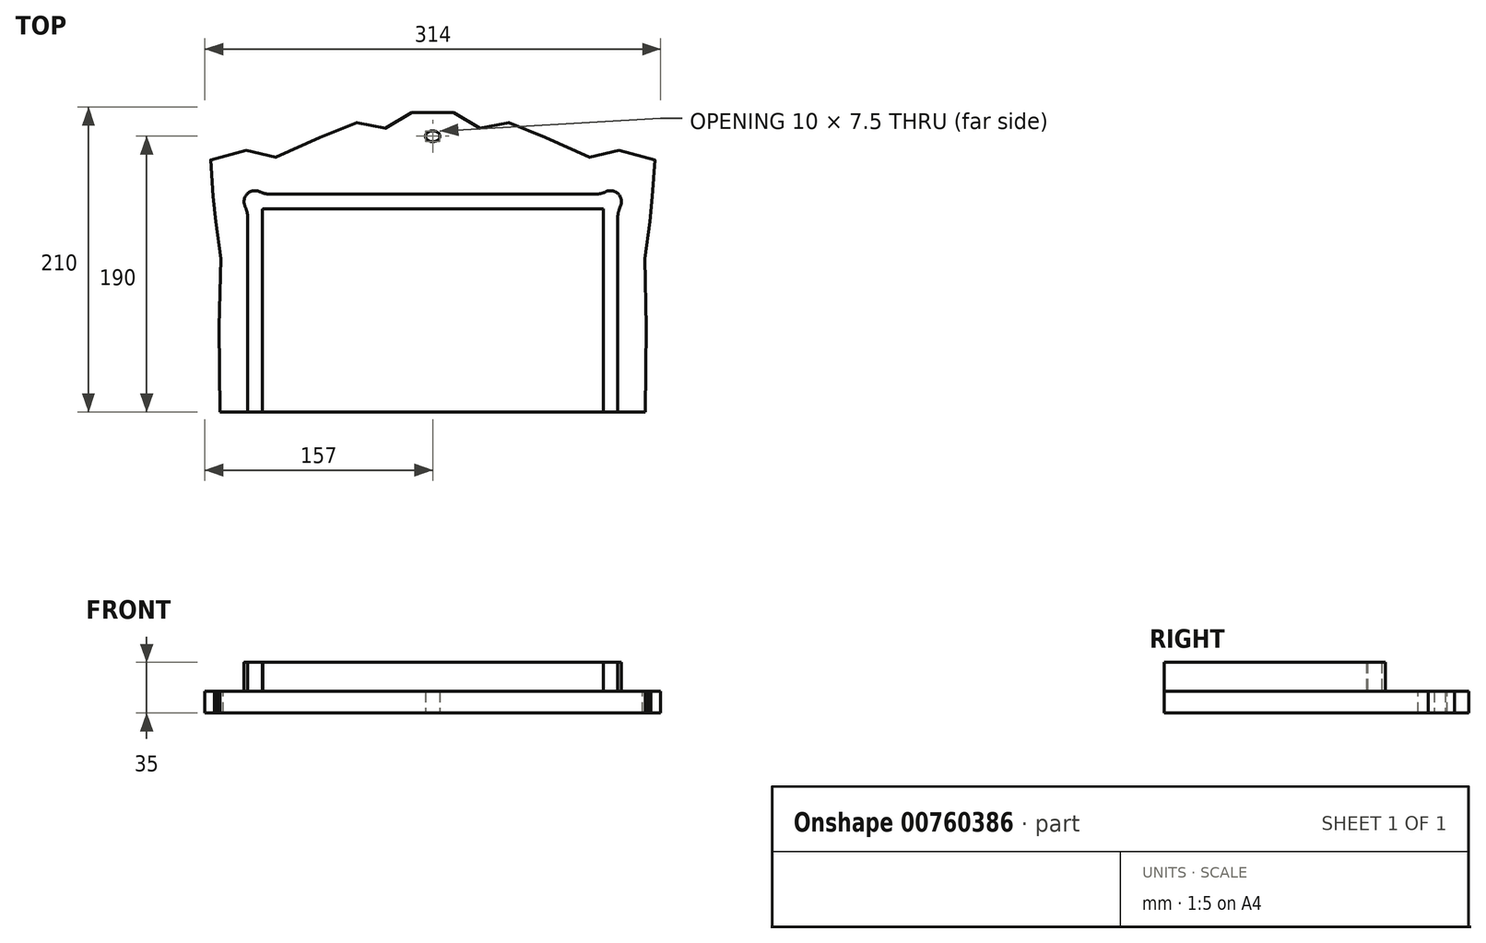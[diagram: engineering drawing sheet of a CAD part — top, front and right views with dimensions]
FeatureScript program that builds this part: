
annotation { "Feature Type Name" : "Feature", "Feature Type Description" : "" }
export const myFeature = defineFeature(function(context is Context, id is Id, definition is map)
    precondition{}
    {
        {
            var Q0;
            Q0=qCreatedBy(makeId("Top.planeOp"),FACE);
            var sketch = newSketch(context, id + "F0", { "sketchPlane" : qUnion([Q0])});
            skPoint(sketch, "E0", {"position": v(151.1, 154.93) * mm});
            skPoint(sketch, "E1", {"position": v(140, 77.47) * mm});
            skPoint(sketch, "E2", {"position": v(146.5, 0) * mm});
            skPoint(sketch, "E3", {"position": v(0, 210) * mm});
            skPoint(sketch, "E4", {"position": v(72.86, 179.48) * mm});
            skPoint(sketch, "E5", {"position": v(-38.35, 186.04) * mm});
            skPoint(sketch, "E6", {"position": v(-24.12, 200) * mm});
            skPoint(sketch, "E7", {"position": v(-154.5, 163.42) * mm});
            skLineSegment(sketch, "E8", {"start": v(0, 210) * mm, "end": v(0, -300) * mm, "construction": true});
            skPoint(sketch, "E9.MirrorP", {"position": v(-72.86, 179.48) * mm});
            skPoint(sketch, "E10.MirrorP", {"position": v(-151.1, 154.93) * mm});
            skPoint(sketch, "E11.MirrorP", {"position": v(-140, 77.47) * mm});
            skPoint(sketch, "E12.MirrorP", {"position": v(-146.5, 0) * mm});
            skPoint(sketch, "E13", {"position": v(0, 0) * mm});
            skPoint(sketch, "E14.MirrorP", {"position": v(154.5, 163.42) * mm});
            skPoint(sketch, "E15.MirrorP", {"position": v(38.35, 186.04) * mm});
            skPoint(sketch, "E16.MirrorP", {"position": v(24.12, 200) * mm});
            skPoint(sketch, "E17", {"position": v(-111.22, 185.44) * mm});
            skPoint(sketch, "E18.MirrorP", {"position": v(111.21, 185.44) * mm});
            skLineSegment(sketch, "E19", {"start": v(-146.5, 0) * mm, "end": v(146.5, 0) * mm});
            skPoint(sketch, "E20", {"position": v(0, 193.84) * mm});
            skPoint(sketch, "E21", {"position": v(-120.16, 190.34) * mm});
            skPoint(sketch, "E22", {"position": v(-131.3, 192.59) * mm});
            skPoint(sketch, "E23", {"position": v(-143.04, 189.12) * mm});
            skPoint(sketch, "E24", {"position": v(-150.16, 182.65) * mm});
            skPoint(sketch, "E25", {"position": v(-153.61, 176.08) * mm});
            skPoint(sketch, "E26", {"position": v(-154.92, 169.2) * mm});
            skPoint(sketch, "E27.MirrorP", {"position": v(120.16, 190.34) * mm});
            skPoint(sketch, "E28.MirrorP", {"position": v(131.3, 192.59) * mm});
            skPoint(sketch, "E29.MirrorP", {"position": v(143.04, 189.12) * mm});
            skPoint(sketch, "E30.MirrorP", {"position": v(150.16, 182.65) * mm});
            skPoint(sketch, "E31.MirrorP", {"position": v(153.61, 176.08) * mm});
            skPoint(sketch, "E32.MirrorP", {"position": v(154.92, 169.2) * mm});
            skFitSpline(sketch, "E33", {"points": [v(-146.5, 0) * mm, v(-140, 77.47) * mm, v(-151.1, 154.93) * mm, v(-154.5, 163.42) * mm, v(-154.92, 169.2) * mm, v(-153.61, 176.08) * mm, v(-150.16, 182.65) * mm, v(-143.04, 189.12) * mm, v(-131.3, 192.59) * mm, v(-120.16, 190.34) * mm, v(-111.22, 185.44) * mm, v(-72.87, 179.48) * mm, v(-38.35, 186.04) * mm, v(-24.12, 200) * mm, v(0, 210) * mm, v(24.12, 200) * mm, v(38.35, 186.04) * mm, v(72.86, 179.48) * mm, v(111.21, 185.44) * mm, v(120.16, 190.34) * mm, v(131.3, 192.59) * mm, v(143.04, 189.12) * mm, v(150.16, 182.65) * mm, v(153.61, 176.08) * mm, v(154.92, 169.2) * mm, v(154.5, 163.42) * mm, v(151.1, 154.93) * mm, v(140, 77.47) * mm, v(146.5, 0) * mm], "startDerivative": vector(163.85, 1049.48) * mm, "endDerivative": vector(163.85, -1049.48) * mm});
            skLineSegment(sketch, "E34.bottom", {"start": v(-107.5, 0) * mm, "end": v(107.5, 0) * mm});
            skSolve(sketch);
        }
        {
            var Q0;
            Q0=qCreatedBy(makeId("Top.planeOp"),FACE);
            cPlane(context, id + "F1", {"entities" : qUnion([Q0]), "cplaneType" : CPlaneType.OFFSET, "offset" : 100 * mm, "width" : 150 * mm, "height" : 150 * mm});
        }
        {
            var Q0;
            Q0=qCreatedBy(id+"F1.planeOp",FACE);
            var sketch = newSketch(context, id + "F2", { "sketchPlane" : qUnion([Q0])});
            skPoint(sketch, "E35.0", {"position": v(-146.5, 0) * mm});
            skPoint(sketch, "E36", {"position": v(-150, 128) * mm});
            skPoint(sketch, "E37", {"position": v(-15, 206) * mm});
            skPoint(sketch, "E38", {"position": v(-83.69, 186) * mm});
            skPoint(sketch, "E39", {"position": v(-57.22, 198) * mm});
            skPoint(sketch, "E40.16.internal.orphan", {"position": v(-102.04, 177) * mm});
            skPoint(sketch, "E40.2.internal.orphan", {"position": v(-147, 60) * mm});
            skLineSegment(sketch, "E41", {"start": v(-146.5, 0) * mm, "end": v(146.5, 0) * mm});
            skLineSegment(sketch, "E42", {"start": v(0, 0) * mm, "end": v(0, 210) * mm, "construction": true});
            skPoint(sketch, "E42.endSnap0", {"position": v(0, 0) * mm});
            skLineSegment(sketch, "E43", {"start": v(214.08, 0) * mm, "end": v(-299.05, 0) * mm, "construction": true});
            skPoint(sketch, "E44.10.internal.orphan", {"position": v(-151, 176) * mm});
            skPoint(sketch, "E44.11.internal.orphan", {"position": v(-138, 182) * mm});
            skPoint(sketch, "E44.12.internal.orphan", {"position": v(-116, 175) * mm});
            skPoint(sketch, "E44.15.internal.orphan", {"position": v(-67.88, 193.66) * mm});
            skPoint(sketch, "E44.17.internal.orphan", {"position": v(-46.27, 200) * mm});
            skPoint(sketch, "E44.18.internal.orphan", {"position": v(-38.42, 198) * mm});
            skPoint(sketch, "E44.19.internal.orphan", {"position": v(-34.04, 196) * mm});
            skPoint(sketch, "E44.2.internal.orphan", {"position": v(-145, 100) * mm});
            skPoint(sketch, "E44.20.internal.orphan", {"position": v(-29, 195) * mm});
            skPoint(sketch, "E44.21.internal.orphan", {"position": v(-25, 198) * mm});
            skPoint(sketch, "E44.3.internal.orphan", {"position": v(-150, 121) * mm});
            skPoint(sketch, "E44.5.internal.orphan", {"position": v(-149, 133) * mm});
            skPoint(sketch, "E44.6.internal.orphan", {"position": v(-147.5, 139) * mm});
            skPoint(sketch, "E44.7.internal.orphan", {"position": v(-149, 145) * mm});
            skPoint(sketch, "E44.8.internal.orphan", {"position": v(-153, 151) * mm});
            skPoint(sketch, "E44.9.internal.orphan", {"position": v(-157, 163) * mm});
            skPoint(sketch, "E45.MirrorP", {"position": v(15, 206) * mm});
            skPoint(sketch, "E46.MirrorP", {"position": v(29, 195) * mm});
            skPoint(sketch, "E47.MirrorP", {"position": v(102.04, 177) * mm});
            skPoint(sketch, "E48.MirrorP", {"position": v(83.69, 186) * mm});
            skPoint(sketch, "E49.MirrorP", {"position": v(46.27, 200) * mm});
            skPoint(sketch, "E50.MirrorP", {"position": v(25, 198) * mm});
            skPoint(sketch, "E51.MirrorP", {"position": v(149, 133) * mm});
            skPoint(sketch, "E52.MirrorP", {"position": v(151, 176) * mm});
            skPoint(sketch, "E53.MirrorP", {"position": v(149, 145) * mm});
            skPoint(sketch, "E54.MirrorP", {"position": v(147, 60) * mm});
            skPoint(sketch, "E55.MirrorP", {"position": v(150, 128) * mm});
            skPoint(sketch, "E56.MirrorP", {"position": v(145, 100) * mm});
            skPoint(sketch, "E57.MirrorP", {"position": v(38.42, 198) * mm});
            skPoint(sketch, "E58.MirrorP", {"position": v(67.88, 193.66) * mm});
            skPoint(sketch, "E59.MirrorP", {"position": v(153, 151) * mm});
            skPoint(sketch, "E60.MirrorP", {"position": v(150, 121) * mm});
            skPoint(sketch, "E61.MirrorP", {"position": v(57.22, 198) * mm});
            skPoint(sketch, "E62.MirrorP", {"position": v(116, 175) * mm});
            skPoint(sketch, "E63.MirrorP", {"position": v(138, 182) * mm});
            skPoint(sketch, "E64.MirrorP", {"position": v(147.5, 139) * mm});
            skPoint(sketch, "E65.MirrorP", {"position": v(157, 163) * mm});
            skPoint(sketch, "E66.MirrorP", {"position": v(34.04, 196) * mm});
            skPoint(sketch, "E67", {"position": v(-123.4, 176.5) * mm});
            skPoint(sketch, "E68", {"position": v(-128, 180) * mm});
            skPoint(sketch, "E69.MirrorP", {"position": v(123.4, 176.5) * mm});
            skPoint(sketch, "E70.MirrorP", {"position": v(128, 180) * mm});
            skFitSpline(sketch, "E71", {"points": [v(-146.5, 0) * mm, v(-147, 60) * mm, v(-145, 100) * mm, v(-150, 121) * mm, v(-150, 128) * mm, v(-149, 133) * mm, v(-147.5, 139) * mm, v(-149, 145) * mm, v(-153, 151) * mm, v(-157, 163) * mm, v(-151, 176) * mm, v(-138, 182) * mm, v(-128, 180) * mm, v(-123.4, 176.5) * mm, v(-116, 175) * mm, v(-102.04, 177) * mm, v(-83.69, 186) * mm, v(-67.88, 193.66) * mm, v(-57.22, 198) * mm, v(-46.27, 200) * mm, v(-38.42, 198) * mm, v(-34.04, 196) * mm, v(-29, 195) * mm, v(-25, 198) * mm, v(-15, 206) * mm, v(0, 210) * mm, v(15, 206) * mm, v(25, 198) * mm, v(29, 195) * mm, v(34.04, 196) * mm, v(38.42, 198) * mm, v(46.27, 200) * mm, v(57.22, 198) * mm, v(67.88, 193.66) * mm, v(83.69, 186) * mm, v(102.04, 177) * mm, v(116, 175) * mm, v(123.4, 176.5) * mm, v(128, 180) * mm, v(138, 182) * mm, v(151, 176) * mm, v(157, 163) * mm, v(153, 151) * mm, v(149, 145) * mm, v(147.5, 139) * mm, v(149, 133) * mm, v(150, 128) * mm, v(150, 121) * mm, v(145, 100) * mm, v(147, 60) * mm, v(146.5, 0) * mm], "startDerivative": vector(-209.03, 1625.36) * mm, "endDerivative": vector(-209.03, -1625.36) * mm});
            skEllipse(sketch, "E72", {"center": v(0, 190) * mm, "majorRadius": 5 * mm, "minorRadius": 3.75 * mm, "majorAxis": v(1, 0)});
            skSolve(sketch);
        }
        {
            var Q0;
            Q0=makeQuery(id+"F2.imprint","IMPRINT",FACE,{"disambiguationData":[TD([[makeQuery(id+"F2.imprint","IMPRINT",EDGE,{"derivedFrom":sQuery(id+"F2.wireOp",EDGE,"E41")}),1.0]])]});
            extrude(context, id + "F3", {"entities" : qUnion([Q0]), "depth" : 15 * mm, "offsetDistance" : 25 * mm});
        }
        {
            var Q0;
            Q0=makeQuery(id+"F3.opExtrude","CAP_FACE",FACE,{"disambiguationData":[OSD([sQuery(id+"F2.wireOp",EDGE,"E41"),sQuery(id+"F2.wireOp",EDGE,"E71")])],"isStart":false});
            var sketch = newSketch(context, id + "F4", { "sketchPlane" : qUnion([Q0])});
            skLineSegment(sketch, "E73.bottom", {"start": v(-127.5, 0) * mm, "end": v(127.5, 0) * mm});
            skLineSegment(sketch, "E73.top", {"start": v(-127.5, 150) * mm, "end": v(127.5, 150) * mm});
            skLineSegment(sketch, "E73.left", {"start": v(-127.5, 0) * mm, "end": v(-127.5, 150) * mm});
            skLineSegment(sketch, "E73.right", {"start": v(127.5, 0) * mm, "end": v(127.5, 150) * mm});
            skLineSegment(sketch, "E74.bottom", {"start": v(-117.5, 0) * mm, "end": v(117.5, 0) * mm});
            skLineSegment(sketch, "E74.top", {"start": v(-117.5, 140) * mm, "end": v(117.5, 140) * mm});
            skLineSegment(sketch, "E74.left", {"start": v(-117.5, 0) * mm, "end": v(-117.5, 140) * mm});
            skLineSegment(sketch, "E74.right", {"start": v(117.5, 0) * mm, "end": v(117.5, 140) * mm});
            skLineSegment(sketch, "E75", {"start": v(-127.5, 150) * mm, "end": v(-117.5, 140) * mm});
            skCircle(sketch, "E76", {"center": v(-122.5, 145) * mm, "radius": 7.5 * mm});
            skCircle(sketch, "E77.MirrorC", {"center": v(122.5, 145) * mm, "radius": 7.5 * mm});
            skSolve(sketch);
        }
        {
            var Q0;
            Q0=makeQuery(id+"F4.imprint","IMPRINT",FACE,{"disambiguationData":[TD([[makeQuery(id+"F4.imprint","IMPRINT",EDGE,{"derivedFrom":sQuery(id+"F4.wireOp",EDGE,"E73.top")}),-1.0]])]});
            var Q1;
            Q1=makeQuery(id+"F4.imprint","IMPRINT",FACE,{"disambiguationData":[TD([[makeQuery(id+"F4.imprint","IMPRINT",EDGE,{"derivedFrom":sQuery(id+"F4.wireOp",EDGE,"E74.bottom")}),1.0]])]});
            var Q2;
            {var subQ0=sQuery(id+"F4.wireOp",EDGE,"E75");Q2=makeQuery(id+"F4.imprint","IMPRINT",FACE,{"disambiguationData":[TD([[makeQuery(id+"F4.imprint","IMPRINT",EDGE,{"derivedFrom":subQ0}),-1.0]])]});}
            var Q3;
            {var subQ1=sQuery(id+"F4.wireOp",EDGE,"E74.top");var subQ3=sQuery(id+"F4.wireOp",EDGE,"E76");var subQ4=makeQuery(id+"F4.imprint","INTERSECT",VERTEX,{"derivedFrom":[subQ1,subQ3]});Q3=makeQuery(id+"F4.imprint","IMPRINT",FACE,{"disambiguationData":[TD([[makeQuery(id+"F4.imprint","IMPRINT",EDGE,{"disambiguationData":[TD([[subQ4,1.0]])],"derivedFrom":subQ3}),1.0]])]});}
            var Q4;
            {var subQ0=sQuery(id+"F4.wireOp",EDGE,"E73.left");var subQ5=sQuery(id+"F4.wireOp",EDGE,"E76");var subQ7=makeQuery(id+"F4.imprint","INTERSECT",VERTEX,{"derivedFrom":[subQ0,subQ5]});Q4=makeQuery(id+"F4.imprint","IMPRINT",FACE,{"disambiguationData":[TD([[makeQuery(id+"F4.imprint","IMPRINT",EDGE,{"disambiguationData":[TD([[subQ7,-1.0]])],"derivedFrom":subQ5}),-1.0]])]});}
            var Q5;
            {var subQ4=sQuery(id+"F4.wireOp",EDGE,"E73.right");Q5=makeQuery(id+"F4.imprint","IMPRINT",FACE,{"disambiguationData":[TD([[makeQuery(id+"F4.imprint","IMPRINT",EDGE,{"derivedFrom":subQ4}),1.0]])]});}
            var Q6;
            {var subQ1=sQuery(id+"F4.wireOp",EDGE,"E73.top");var subQ3=sQuery(id+"F4.wireOp",EDGE,"E76");var subQ4=makeQuery(id+"F4.imprint","INTERSECT",VERTEX,{"derivedFrom":[subQ1,subQ3]});Q6=makeQuery(id+"F4.imprint","IMPRINT",FACE,{"disambiguationData":[TD([[makeQuery(id+"F4.imprint","IMPRINT",EDGE,{"disambiguationData":[TD([[subQ4,-1.0]])],"derivedFrom":subQ3}),1.0]])]});}
            var Q7;
            {var subQ6=sQuery(id+"F4.wireOp",EDGE,"E73.right");var subQ8=sQuery(id+"F4.wireOp",EDGE,"E73.top");var subQ9=makeQuery(id+"F4.imprint","INTERSECT",VERTEX,{"derivedFrom":[subQ8,subQ6]});Q7=makeQuery(id+"F4.imprint","IMPRINT",FACE,{"disambiguationData":[TD([[makeQuery(id+"F4.imprint","IMPRINT",EDGE,{"disambiguationData":[TD([[subQ9,1.0]])],"derivedFrom":subQ8}),-1.0]])]});}
            var Q8;
            {var subQ0=sQuery(id+"F4.wireOp",EDGE,"E73.right");var subQ1=sQuery(id+"F4.wireOp",EDGE,"E73.top");var subQ2=makeQuery(id+"F4.imprint","INTERSECT",VERTEX,{"derivedFrom":[subQ1,subQ0]});Q8=makeQuery(id+"F4.imprint","IMPRINT",FACE,{"disambiguationData":[TD([[makeQuery(id+"F4.imprint","IMPRINT",EDGE,{"disambiguationData":[TD([[subQ2,1.0]])],"derivedFrom":subQ1}),1.0]])]});}
            extrude(context, id + "F5", {"entities" : qUnion([Q0, Q1, Q2, Q3, Q4, Q5, Q6, Q7, Q8]), "depth" : 10 * mm, "offsetDistance" : 25 * mm});
        }
        {
            var Q0;
            Q0=makeQuery(id+"F5.opExtrude","SWEPT_EDGE",EDGE,{"disambiguationData":[OSD([sQuery(id+"F4.wireOp",EDGE,"E73.top"),sQuery(id+"F4.wireOp",EDGE,"E76")])]});
            var Q1;
            Q1=makeQuery(id+"F5.opExtrude","SWEPT_EDGE",EDGE,{"disambiguationData":[OSD([sQuery(id+"F4.wireOp",EDGE,"E73.left"),sQuery(id+"F4.wireOp",EDGE,"E76")])]});
            var Q2;
            Q2=makeQuery(id+"F5.opExtrude","SWEPT_EDGE",EDGE,{"disambiguationData":[OSD([sQuery(id+"F4.wireOp",EDGE,"E73.top"),sQuery(id+"F4.wireOp",EDGE,"E77.MirrorC")])]});
            var Q3;
            Q3=makeQuery(id+"F5.opExtrude","SWEPT_EDGE",EDGE,{"disambiguationData":[OSD([sQuery(id+"F4.wireOp",EDGE,"E73.right"),sQuery(id+"F4.wireOp",EDGE,"E77.MirrorC")])]});
            fillet(context, id + "F6", {"entities" : qUnion([Q0, Q1, Q2, Q3]), "radius" : 20 * mm, "tangentPropagation" : true, "allowEdgeOverflow" : false});
        }
        {
            var Q0;
            Q0=makeQuery(id+"F5.opExtrude","CAP_FACE",FACE,{"disambiguationData":[OSD([sQuery(id+"F01OqzFfX9itPD7_1.wireOp",EDGE,"TDFwYFJC-9rLf-SEpr-LMun-f7n9ZEvJ4hNh"),sQuery(id+"F01OqzFfX9itPD7_1.wireOp",EDGE,"fCgicrGS-55NG-sWUy-wnvS-e9e9rh1w3ghR"),sQuery(id+"F01OqzFfX9itPD7_1.wireOp",EDGE,"5ItRyK9n-nWWQ-e84D-iQgI-aiFtkuca7bxh"),sQuery(id+"F4.wireOp",EDGE,"E73.bottom"),sQuery(id+"F4.wireOp",EDGE,"E73.top"),sQuery(id+"F4.wireOp",EDGE,"E73.left"),sQuery(id+"F4.wireOp",EDGE,"E73.right"),sQuery(id+"F4.wireOp",EDGE,"E74.bottom")])],"isStart":false});
            var sketch = newSketch(context, id + "F7", { "sketchPlane" : qUnion([Q0])});
            skLineSegment(sketch, "E78.0", {"start": v(117.5, 0) * mm, "end": v(117.5, 140) * mm});
            skLineSegment(sketch, "E79.0", {"start": v(-117.5, 140) * mm, "end": v(117.5, 140) * mm});
            skLineSegment(sketch, "E80.0", {"start": v(-117.5, 0) * mm, "end": v(-117.5, 140) * mm});
            skLineSegment(sketch, "E81.0", {"start": v(-117.5, 0) * mm, "end": v(117.5, 0) * mm});
            skPoint(sketch, "E82.orphan", {"position": v(-117.5, 140) * mm});
            skSolve(sketch);
        }
        {
            var Q0;
            {var subQ0=sQuery(id+"F7.wireOp",EDGE,"E80.0");Q0=makeQuery(id+"F7.imprint","IMPRINT",FACE,{"disambiguationData":[TD([[makeQuery(id+"F7.imprint","IMPRINT",EDGE,{"derivedFrom":subQ0}),-1.0]])]});}
            var Q1;
            {var subQ0=sQuery(id+"F7.wireOp",EDGE,"eHPwFbGt-x49O-upP5-2J7X-MqRqS1DIb1iX");var subQ1=makeQuery(id+"F7.imprint","INTERSECT",VERTEX,{"derivedFrom":[sQuery(id+"F7.wireOp",EDGE,"E79.0"),subQ0]});Q1=makeQuery(id+"F7.imprint","IMPRINT",FACE,{"disambiguationData":[TD([[makeQuery(id+"F7.imprint","IMPRINT",EDGE,{"disambiguationData":[TD([[subQ1,-1.0]])],"derivedFrom":subQ0}),1.0]])]});}
            var Q2;
            {var subQ1=sQuery(id+"F7.wireOp",EDGE,"E78.0");var subQ6=sQuery(id+"F7.wireOp",EDGE,"a167e5de-4d74-4f45-bc02-d425cc1066e10.MirrorC");var subQ9=makeQuery(id+"F7.imprint","INTERSECT",VERTEX,{"derivedFrom":[subQ1,subQ6]});Q2=makeQuery(id+"F7.imprint","IMPRINT",FACE,{"disambiguationData":[TD([[makeQuery(id+"F7.imprint","IMPRINT",EDGE,{"disambiguationData":[TD([[subQ9,1.0]])],"derivedFrom":subQ6}),-1.0]])]});}
            var Q3;
            {var subQ1=sQuery(id+"F4.wireOp",EDGE,"E77.MirrorC");var subQ2=makeQuery(id+"F5.opExtrude","CAP_EDGE",EDGE,{"disambiguationData":[OSD([subQ1]),TDD([makeQuery(id+"F4.imprint","IMPRINT",EDGE,{"disambiguationData":[TD([[makeQuery(id+"F4.imprint","INTERSECT",VERTEX,{"derivedFrom":[sQuery(id+"F4.wireOp",EDGE,"E74.top"),subQ1]}),1.0]])],"derivedFrom":subQ1})])],"isStart":false});Q3=makeQuery(id+"F7.imprint","IMPRINT",FACE,{"disambiguationData":[TD([[makeQuery(id+"F7.imprint","IMPRINT",EDGE,{"derivedFrom":subQ2}),1.0]])]});}
            var Q4;
            {var subQ0=sQuery(id+"F7.wireOp",EDGE,"c7arcQw8-U9WH-50iv-UKyZ-HqhImG9bkcTv");var subQ1=makeQuery(id+"F7.imprint","INTERSECT",VERTEX,{"derivedFrom":[sQuery(id+"F7.wireOp",EDGE,"E79.0"),subQ0]});Q4=makeQuery(id+"F7.imprint","IMPRINT",FACE,{"disambiguationData":[TD([[makeQuery(id+"F7.imprint","IMPRINT",EDGE,{"disambiguationData":[TD([[subQ1,-1.0]])],"derivedFrom":subQ0}),1.0]])]});}
            var Q5;
            {var subQ1=sQuery(id+"F7.wireOp",EDGE,"E78.0");var subQ6=sQuery(id+"F7.wireOp",EDGE,"c4ad2870-bfd3-4a91-94f6-d68b5c8148240.MirrorC");var subQ9=makeQuery(id+"F7.imprint","INTERSECT",VERTEX,{"derivedFrom":[subQ1,subQ6]});Q5=makeQuery(id+"F7.imprint","IMPRINT",FACE,{"disambiguationData":[TD([[makeQuery(id+"F7.imprint","IMPRINT",EDGE,{"disambiguationData":[TD([[subQ9,1.0]])],"derivedFrom":subQ6}),-1.0]])]});}
            extrude(context, id + "F8", {"entities" : qUnion([Q0, Q1, Q2, Q3, Q4, Q5]), "operationType" : NewBodyOperationType.ADD, "depth" : 10 * mm, "offsetDistance" : 25 * mm});
        }
        {
            var Q0;
            Q0=makeQuery(id+"F8.opExtrude","CAP_FACE",FACE,{"disambiguationData":[OSD([sQuery(id+"F4.wireOp",EDGE,"E77.MirrorC"),sQuery(id+"F7.wireOp",EDGE,"E78.0"),sQuery(id+"F7.wireOp",EDGE,"E79.0"),sQuery(id+"F7.wireOp",EDGE,"E80.0"),sQuery(id+"F7.wireOp",EDGE,"E81.0")])],"isStart":false});
            var sketch = newSketch(context, id + "F9", { "sketchPlane" : qUnion([Q0])});
            skLineSegment(sketch, "E83", {"start": v(-107.5, 0) * mm, "end": v(-107.5, 130) * mm});
            skLineSegment(sketch, "E84", {"start": v(-107.5, 130) * mm, "end": v(107.5, 130) * mm});
            skLineSegment(sketch, "E85", {"start": v(107.5, 130) * mm, "end": v(107.5, 0) * mm});
            skLineSegment(sketch, "E86", {"start": v(107.5, 0) * mm, "end": v(-107.5, 0) * mm});
            skSolve(sketch);
        }
        {
            var Q0;
            Q0=makeQuery(id+"F9.imprint","IMPRINT",FACE,{"disambiguationData":[TD([[makeQuery(id+"F9.imprint","IMPRINT",EDGE,{"derivedFrom":sQuery(id+"F9.wireOp",EDGE,"E83")}),-1.0]])]});
            extrude(context, id + "F10", {"entities" : qUnion([Q0]), "operationType" : NewBodyOperationType.REMOVE, "oppositeDirection" : true, "depth" : 10 * mm, "offsetDistance" : 25 * mm});
        }
    });
